# Revit family: Clarus_beWall_R18
name_source: partatom
category: Furniture
revit_build: Autodesk Revit 2018 (Build: 20190510_1515(x64)
units: mm (PartAtom-declared; Revit-internal decimal feet)

## family parameters
Cut with Voids When Loaded = No
Host = Face
Room Calculation Point = No
Shared = No

## types (1)
- 67 3/8" X 40"
    Default Elevation = 0"
    Depth = 1 1/2"
    Description = The simple and elegant be! Wall glassboard puts your best ideas on display.
The cleanly designed be! Wall comes in one standard size with a selection
of two core fi nishes and boasts magnetic glass, radiused corners, and added
depth to prevent marker smudges and stains on your wall. The small acoustic
panel is ideal for tacking up important items such as photos, notes, or fabric
samples to enhance your most creative brainstorm sessions. Easily installed
with the Clarus® TruMount™ system, the be! Wall can be hung horizontally
or vertically, accommodating any modern-day work environment. With be!
Wall, everyone can collaborate without breaking the bank.
    Height = 40"
    Manufacturer = Clarus
    Model = be! Wall
    Modeled By = Commense Studio
    Product URL = https://www.clarus.com
    URL = https://www.clarus.com
    Width = 67 3/8"

## geometry (parser evidence)
native form markers: Sweep x2
no freeform markers — native parametric forms only
